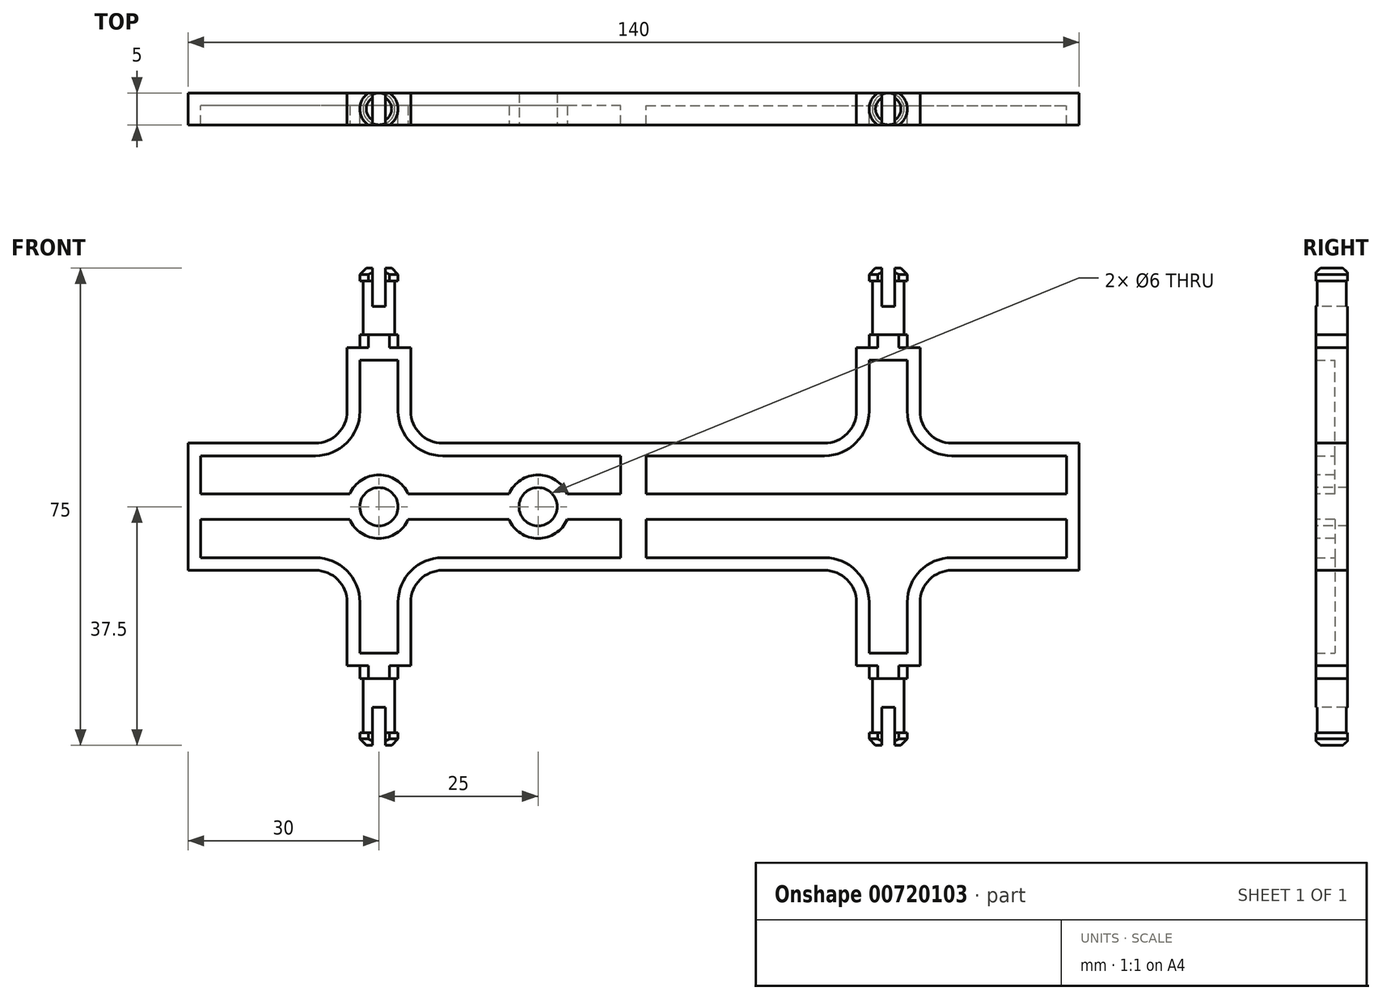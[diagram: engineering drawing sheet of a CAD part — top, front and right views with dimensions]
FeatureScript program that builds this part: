
annotation { "Feature Type Name" : "Feature", "Feature Type Description" : "" }
export const myFeature = defineFeature(function(context is Context, id is Id, definition is map)
    precondition{}
    {
        {
            var Q0;
            Q0=qCreatedBy(makeId("Front.planeOp"),FACE);
            var sketch = newSketch(context, id + "F0", { "sketchPlane" : qUnion([Q0])});
            skLineSegment(sketch, "E0.bottom", {"start": v(0, 0) * mm, "end": v(70, 0) * mm});
            skLineSegment(sketch, "E0.top", {"start": v(0, 10) * mm, "end": v(30, 10) * mm});
            skLineSegment(sketch, "E0.left", {"start": v(0, 0) * mm, "end": v(0, 10) * mm});
            skLineSegment(sketch, "E0.right", {"start": v(70, 0) * mm, "end": v(70, 10) * mm});
            skLineSegment(sketch, "E1.top", {"start": v(35, 25) * mm, "end": v(45, 25) * mm});
            skLineSegment(sketch, "E1.left", {"start": v(35, 15) * mm, "end": v(35, 25) * mm});
            skLineSegment(sketch, "E1.right", {"start": v(45, 15) * mm, "end": v(45, 25) * mm});
            skLineSegment(sketch, "E2.trimOffspring", {"start": v(50, 10) * mm, "end": v(70, 10) * mm});
            skPoint(sketch, "E3.visualSharp", {"position": v(35, 10) * mm});
            skArc(sketch, "E3.filletArc", {"start": v(30, 10) * mm, "mid": v(33.54, 11.46) * mm, "end": v(35, 15) * mm});
            skPoint(sketch, "E4.visualSharp", {"position": v(45, 10) * mm});
            skArc(sketch, "E4.filletArc", {"start": v(45, 15) * mm, "mid": v(46.46, 11.46) * mm, "end": v(50, 10) * mm});
            skSolve(sketch);
        }
        {
            var Q0;
            Q0=makeQuery(id+"F0.imprint","IMPRINT",FACE,{"disambiguationData":[TD([[makeQuery(id+"F0.imprint","IMPRINT",EDGE,{"derivedFrom":sQuery(id+"F0.wireOp",EDGE,"E0.bottom")}),1.0]])]});
            extrude(context, id + "F1", {"entities" : qUnion([Q0]), "endBound" : BoundingType.SYMMETRIC, "depth" : 5 * mm, "offsetDistance" : 25 * mm});
        }
        {
            var Q0;
            Q0=makeQuery(id+"F1.opExtrude","CAP_FACE",FACE,{"disambiguationData":[OSD([sQuery(id+"F0.wireOp",EDGE,"E0.bottom"),sQuery(id+"F0.wireOp",EDGE,"E0.top"),sQuery(id+"F0.wireOp",EDGE,"E0.left"),sQuery(id+"F0.wireOp",EDGE,"E0.right"),sQuery(id+"F0.wireOp",EDGE,"E1.top"),sQuery(id+"F0.wireOp",EDGE,"E1.left"),sQuery(id+"F0.wireOp",EDGE,"E1.right"),sQuery(id+"F0.wireOp",EDGE,"E2.trimOffspring"),sQuery(id+"F0.wireOp",EDGE,"E3.filletArc"),sQuery(id+"F0.wireOp",EDGE,"E4.filletArc")])],"isStart":false});
            shell(context, id + "F2", {"entities" : qUnion([Q0]), "thickness" : 2 * mm});
        }
        {
            var Q0;
            Q0=qCreatedBy(makeId("Front.planeOp"),FACE);
            var sketch = newSketch(context, id + "F3", { "sketchPlane" : qUnion([Q0])});
            skLineSegment(sketch, "E5", {"start": v(40, 25) * mm, "end": v(40, 37.5) * mm});
            skLineSegment(sketch, "E6", {"start": v(40, 37.5) * mm, "end": v(37, 37.5) * mm});
            skLineSegment(sketch, "E7", {"start": v(37, 37.5) * mm, "end": v(37, 35.5) * mm});
            skLineSegment(sketch, "E8", {"start": v(37, 35.5) * mm, "end": v(37.5, 35.5) * mm});
            skLineSegment(sketch, "E9", {"start": v(37.5, 35.5) * mm, "end": v(37.5, 27) * mm});
            skLineSegment(sketch, "E10", {"start": v(37.5, 27) * mm, "end": v(37, 27) * mm});
            skLineSegment(sketch, "E11", {"start": v(37, 27) * mm, "end": v(37, 25) * mm});
            skLineSegment(sketch, "E12", {"start": v(37, 25) * mm, "end": v(40, 25) * mm});
            skSolve(sketch);
        }
        {
            var Q0;
            Q0=makeQuery(id+"F3.imprint","IMPRINT",FACE,{"disambiguationData":[TD([[makeQuery(id+"F3.imprint","IMPRINT",EDGE,{"derivedFrom":sQuery(id+"F3.wireOp",EDGE,"E5")}),1.0]])]});
            var Q1;
            Q1=sQuery(id+"F3.wireOp",EDGE,"E5");
            revolve(context, id + "F4", {"operationType" : NewBodyOperationType.ADD, "surfaceOperationType" : NewSurfaceOperationType.NEW, "entities" : qUnion([Q0]), "axis" : qUnion([Q1]), "revolveType" : RevolveType.FULL});
        }
        {
            var Q0;
            Q0=makeQuery(id+"F4.opRevolve","SWEPT_EDGE",EDGE,{"disambiguationData":[OSD([sQuery(id+"F3.wireOp",EDGE,"E6"),sQuery(id+"F3.wireOp",EDGE,"E7")])]});
            chamfer(context, id + "F5", {"entities" : qUnion([Q0]), "width" : 1 * mm, "tangentPropagation" : true});
        }
        {
            var Q0;
            Q0=makeQuery(id+"F4.opRevolve","SWEPT_FACE",FACE,{"disambiguationData":[OSD([sQuery(id+"F3.wireOp",EDGE,"E6")])]});
            var sketch = newSketch(context, id + "F6", { "sketchPlane" : qUnion([Q0])});
            skLineSegment(sketch, "E13.bottom", {"start": v(-2.4, 2.5) * mm, "end": v(72.6, 2.5) * mm});
            skLineSegment(sketch, "E13.top", {"start": v(-2.4, -2.5) * mm, "end": v(72.6, -2.5) * mm});
            skLineSegment(sketch, "E13.left", {"start": v(-2.4, 2.5) * mm, "end": v(-2.4, -2.5) * mm});
            skLineSegment(sketch, "E13.right", {"start": v(72.6, 2.5) * mm, "end": v(72.6, -2.5) * mm});
            skSolve(sketch);
        }
        {
            var Q0;
            Q0 = qSketchRegion(id + "F6", true);
            extrude(context, id + "F7", {"entities" : qUnion([Q0]), "operationType" : NewBodyOperationType.INTERSECT, "endBound" : BoundingType.THROUGH_ALL, "oppositeDirection" : true, "depth" : 25 * mm, "offsetDistance" : 25 * mm});
        }
        {
            var Q0;
            Q0=makeQuery(id+"F4.opRevolve","SWEPT_FACE",FACE,{"disambiguationData":[OSD([sQuery(id+"F3.wireOp",EDGE,"E6")])]});
            var sketch = newSketch(context, id + "F8", { "sketchPlane" : qUnion([Q0])});
            skLineSegment(sketch, "E14.bottom", {"start": v(39, 3.52) * mm, "end": v(41, 3.52) * mm});
            skLineSegment(sketch, "E14.top", {"start": v(39, -3.68) * mm, "end": v(41, -3.68) * mm});
            skLineSegment(sketch, "E14.left", {"start": v(39, 3.52) * mm, "end": v(39, -3.68) * mm});
            skLineSegment(sketch, "E14.right", {"start": v(41, 3.52) * mm, "end": v(41, -3.68) * mm});
            skSolve(sketch);
        }
        {
            var Q0;
            Q0 = qSketchRegion(id + "F8", true);
            extrude(context, id + "F9", {"entities" : qUnion([Q0]), "operationType" : NewBodyOperationType.REMOVE, "oppositeDirection" : true, "depth" : 6 * mm, "offsetDistance" : 25 * mm});
        }
        {
            var Q0;
            Q0=makeQuery(id+"F1.opExtrude","SWEPT_BODY",BODY,{"disambiguationData":[OSD([sQuery(id+"F0.wireOp",EDGE,"E0.bottom"),sQuery(id+"F0.wireOp",EDGE,"E0.top"),sQuery(id+"F0.wireOp",EDGE,"E0.left"),sQuery(id+"F0.wireOp",EDGE,"E0.right"),sQuery(id+"F0.wireOp",EDGE,"E1.top"),sQuery(id+"F0.wireOp",EDGE,"E1.left"),sQuery(id+"F0.wireOp",EDGE,"E1.right"),sQuery(id+"F0.wireOp",EDGE,"E2.trimOffspring"),sQuery(id+"F0.wireOp",EDGE,"E3.filletArc"),sQuery(id+"F0.wireOp",EDGE,"E4.filletArc")])]});
            var Q1;
            Q1=makeQuery(id+"F1.opExtrude","SWEPT_FACE",FACE,{"disambiguationData":[OSD([sQuery(id+"F0.wireOp",EDGE,"E0.bottom")])]});
            mirror(context, id + "F10", {"operationType" : NewBodyOperationType.ADD, "entities" : qUnion([Q0]), "mirrorPlane" : qUnion([Q1])});
        }
        {
            var Q0;
            Q0=makeQuery(id+"F1.opExtrude","SWEPT_BODY",BODY,{"disambiguationData":[OSD([sQuery(id+"F0.wireOp",EDGE,"E0.bottom"),sQuery(id+"F0.wireOp",EDGE,"E0.top"),sQuery(id+"F0.wireOp",EDGE,"E0.left"),sQuery(id+"F0.wireOp",EDGE,"E0.right"),sQuery(id+"F0.wireOp",EDGE,"E1.top"),sQuery(id+"F0.wireOp",EDGE,"E1.left"),sQuery(id+"F0.wireOp",EDGE,"E1.right"),sQuery(id+"F0.wireOp",EDGE,"E2.trimOffspring"),sQuery(id+"F0.wireOp",EDGE,"E3.filletArc"),sQuery(id+"F0.wireOp",EDGE,"E4.filletArc")])]});
            var Q1;
            {var subQ0=makeQuery(id+"F1.opExtrude","SWEPT_FACE",FACE,{"disambiguationData":[OSD([sQuery(id+"F0.wireOp",EDGE,"E0.left")])]});Q1=makeQuery(id+"F10.boolean.opBoolean","MERGE",FACE,{"derivedFrom":[subQ0,makeQuery(id+"F10.opPattern","COPY",FACE,{"derivedFrom":subQ0,"instanceName":"1"})]});}
            mirror(context, id + "F11", {"operationType" : NewBodyOperationType.ADD, "entities" : qUnion([Q0]), "mirrorPlane" : qUnion([Q1])});
        }
        {
            var Q0;
            {var subQ0=makeQuery(id+"F7.boolean.opBoolean","MERGE",FACE,{"derivedFrom":[makeQuery(id+"F1.opExtrude","CAP_FACE",FACE,{"disambiguationData":[OSD([sQuery(id+"F0.wireOp",EDGE,"E0.bottom"),sQuery(id+"F0.wireOp",EDGE,"E0.top"),sQuery(id+"F0.wireOp",EDGE,"E0.left"),sQuery(id+"F0.wireOp",EDGE,"E0.right"),sQuery(id+"F0.wireOp",EDGE,"E1.top"),sQuery(id+"F0.wireOp",EDGE,"E1.left"),sQuery(id+"F0.wireOp",EDGE,"E1.right"),sQuery(id+"F0.wireOp",EDGE,"E2.trimOffspring"),sQuery(id+"F0.wireOp",EDGE,"E3.filletArc"),sQuery(id+"F0.wireOp",EDGE,"E4.filletArc")])],"isStart":false}),makeQuery(id+"F7.boolean.toolComplement.opBoolean","COPY",FACE,{"derivedFrom":makeQuery(id+"F7.opExtrude","SWEPT_FACE",FACE,{"disambiguationData":[OSD([sQuery(id+"F6.wireOp",EDGE,"E13.top")])]})})]});var subQ1=makeQuery(id+"F10.boolean.opBoolean","MERGE",FACE,{"derivedFrom":[subQ0,makeQuery(id+"F10.opPattern","COPY",FACE,{"derivedFrom":subQ0,"instanceName":"1"})]});Q0=makeQuery(id+"F11.boolean.opBoolean","MERGE",FACE,{"derivedFrom":[subQ1,makeQuery(id+"F11.opPattern","COPY",FACE,{"derivedFrom":subQ1,"instanceName":"1"})]});}
            var sketch = newSketch(context, id + "F12", { "sketchPlane" : qUnion([Q0])});
            skCircle(sketch, "E15", {"center": v(-40, 0) * mm, "radius": 5 * mm});
            skCircle(sketch, "E16", {"center": v(-15, 0) * mm, "radius": 5 * mm});
            skSolve(sketch);
        }
        {
            var Q0;
            Q0 = qSketchRegion(id + "F12", true);
            extrude(context, id + "F13", {"entities" : qUnion([Q0]), "operationType" : NewBodyOperationType.ADD, "endBound" : BoundingType.UP_TO_NEXT, "oppositeDirection" : true, "depth" : 25 * mm, "offsetDistance" : 25 * mm});
        }
        {
            var Q0;
            {var subQ0=makeQuery(id+"F7.boolean.opBoolean","MERGE",FACE,{"derivedFrom":[makeQuery(id+"F1.opExtrude","CAP_FACE",FACE,{"disambiguationData":[OSD([sQuery(id+"F0.wireOp",EDGE,"E0.bottom"),sQuery(id+"F0.wireOp",EDGE,"E0.top"),sQuery(id+"F0.wireOp",EDGE,"E0.left"),sQuery(id+"F0.wireOp",EDGE,"E0.right"),sQuery(id+"F0.wireOp",EDGE,"E1.top"),sQuery(id+"F0.wireOp",EDGE,"E1.left"),sQuery(id+"F0.wireOp",EDGE,"E1.right"),sQuery(id+"F0.wireOp",EDGE,"E2.trimOffspring"),sQuery(id+"F0.wireOp",EDGE,"E3.filletArc"),sQuery(id+"F0.wireOp",EDGE,"E4.filletArc")])],"isStart":false}),makeQuery(id+"F7.boolean.toolComplement.opBoolean","COPY",FACE,{"derivedFrom":makeQuery(id+"F7.opExtrude","SWEPT_FACE",FACE,{"disambiguationData":[OSD([sQuery(id+"F6.wireOp",EDGE,"E13.top")])]})})]});var subQ1=makeQuery(id+"F10.boolean.opBoolean","MERGE",FACE,{"derivedFrom":[subQ0,makeQuery(id+"F10.opPattern","COPY",FACE,{"derivedFrom":subQ0,"instanceName":"1"})]});Q0=makeQuery(id+"F13.boolean.opBoolean","MERGE",FACE,{"derivedFrom":[makeQuery(id+"F11.boolean.opBoolean","MERGE",FACE,{"derivedFrom":[subQ1,makeQuery(id+"F11.opPattern","COPY",FACE,{"derivedFrom":subQ1,"instanceName":"1"})]}),makeQuery(id+"F13.opExtrude","CAP_FACE",FACE,{"disambiguationData":[OSD([sQuery(id+"F12.wireOp",EDGE,"E15")])],"isStart":true}),makeQuery(id+"F13.opExtrude","CAP_FACE",FACE,{"disambiguationData":[OSD([sQuery(id+"F12.wireOp",EDGE,"E16")])],"isStart":true})]});}
            var sketch = newSketch(context, id + "F14", { "sketchPlane" : qUnion([Q0])});
            skPoint(sketch, "E17", {"position": v(-40, 0) * mm});
            skPoint(sketch, "E18", {"position": v(-15, 0) * mm});
            skSolve(sketch);
        }
        {
            var Q0;
            Q0=sQuery(id+"F14.wireOp",VERTEX,"E17");
            var Q1;
            Q1=sQuery(id+"F14.wireOp",VERTEX,"E18");
            var Q2;
            Q2=makeQuery(id+"F1.opExtrude","SWEPT_BODY",BODY,{"disambiguationData":[OSD([sQuery(id+"F0.wireOp",EDGE,"E0.bottom"),sQuery(id+"F0.wireOp",EDGE,"E0.top"),sQuery(id+"F0.wireOp",EDGE,"E0.left"),sQuery(id+"F0.wireOp",EDGE,"E0.right"),sQuery(id+"F0.wireOp",EDGE,"E1.top"),sQuery(id+"F0.wireOp",EDGE,"E1.left"),sQuery(id+"F0.wireOp",EDGE,"E1.right"),sQuery(id+"F0.wireOp",EDGE,"E2.trimOffspring"),sQuery(id+"F0.wireOp",EDGE,"E3.filletArc"),sQuery(id+"F0.wireOp",EDGE,"E4.filletArc")])]});
            hole(context, id + "F15", {"style" : HoleStyle.SIMPLE, "endStyle" : HoleEndStyle.THROUGH, "holeDiameter" : 6 * mm, "majorDiameter" : 5 * mm, "isTappedThrough" : true, "tappedDepth" : 12 * mm, "tapClearance" : 3, "locations" : qUnion([Q0, Q1]), "scope" : qUnion([Q2])});
        }
    });
